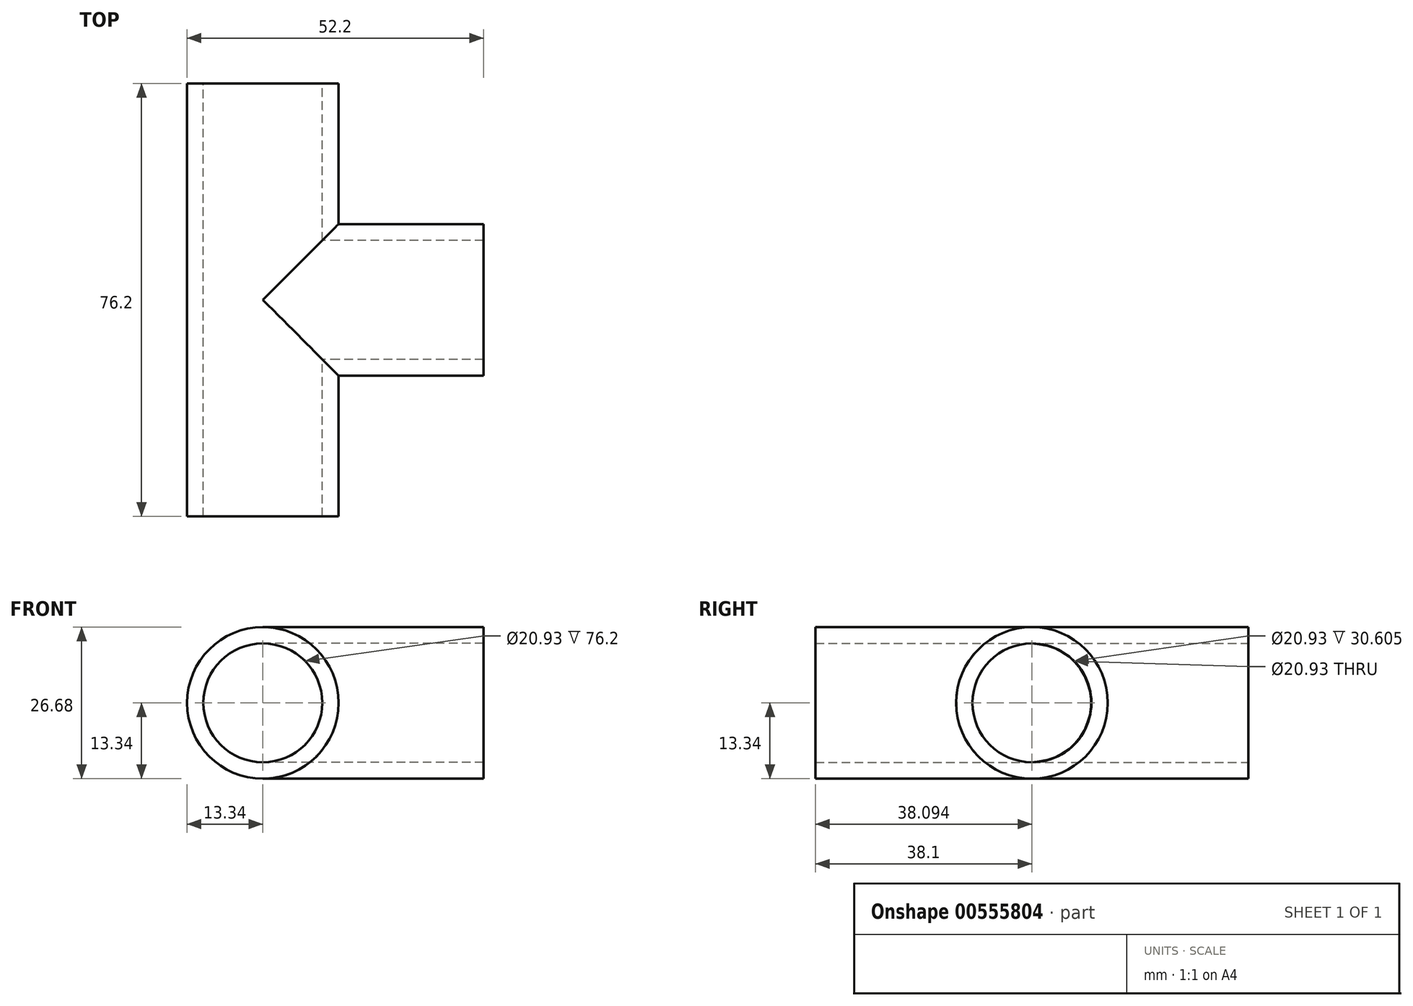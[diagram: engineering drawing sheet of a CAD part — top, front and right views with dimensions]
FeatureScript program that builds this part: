
annotation { "Feature Type Name" : "Feature", "Feature Type Description" : "" }
export const myFeature = defineFeature(function(context is Context, id is Id, definition is map)
    precondition{}
    {
        {
            var Q0;
            Q0=qCreatedBy(makeId("Front.planeOp"),FACE);
            var sketch = newSketch(context, id + "F0", { "sketchPlane" : qUnion([Q0])});
            skCircle(sketch, "E0", {"center": v(0, 0) * mm, "radius": 13.33 * mm});
            skCircle(sketch, "E1", {"center": v(0, 0) * mm, "radius": 10.46 * mm});
            skSolve(sketch);
        }
        {
            var Q0;
            Q0=qCreatedBy(makeId("Right.planeOp"),FACE);
            var sketch = newSketch(context, id + "F1", { "sketchPlane" : qUnion([Q0])});
            skLineSegment(sketch, "E2", {"start": v(0, 0) * mm, "end": v(76.2, 0) * mm});
            skSolve(sketch);
        }
        {
            var Q0;
            Q0=makeQuery(id+"F0.imprint","IMPRINT",FACE,{"disambiguationData":[TD([[makeQuery(id+"F0.imprint","IMPRINT",EDGE,{"derivedFrom":sQuery(id+"F0.wireOp",EDGE,"E0")}),1.0]])]});
            var Q1;
            Q1=sQuery(id+"F1.wireOp",EDGE,"E2");
            sweep(context, id + "F2", {"profiles" : qUnion([Q0]), "path" : qUnion([Q1])});
        }
        {
            var Q0;
            Q0=qCreatedBy(makeId("Right.planeOp"),FACE);
            var sketch = newSketch(context, id + "F3", { "sketchPlane" : qUnion([Q0])});
            skLineSegment(sketch, "E3.left", {"start": v(76.19, -14.7) * mm, "end": v(76.19, 11.97) * mm, "construction": true});
            skPoint(sketch, "E3.middle", {"position": v(0, 0) * mm});
            skLineSegment(sketch, "E4", {"start": v(0, -13.33) * mm, "end": v(0, 13.34) * mm, "construction": true});
            skPoint(sketch, "E3.right.end.orphan", {"position": v(-76.19, 14.7) * mm});
            skPoint(sketch, "E3.right.start.orphan", {"position": v(-76.19, -11.97) * mm});
            skLineSegment(sketch, "E5", {"start": v(0, -13.33) * mm, "end": v(76.19, -13.33) * mm, "construction": true});
            skLineSegment(sketch, "E6", {"start": v(0, 13.34) * mm, "end": v(76.2, 13.34) * mm, "construction": true});
            skLineSegment(sketch, "E7", {"start": v(76.2, 13.34) * mm, "end": v(76.19, -13.33) * mm, "construction": true});
            skLineSegment(sketch, "E8", {"start": v(0, 0) * mm, "end": v(76.19, 0) * mm, "construction": true});
            skCircle(sketch, "E9", {"center": v(38.1, 0) * mm, "radius": 10.46 * mm});
            skSolve(sketch);
        }
        {
            var Q0;
            Q0 = qSketchRegion(id + "F3", true);
            extrude(context, id + "F4", {"entities" : qUnion([Q0]), "operationType" : NewBodyOperationType.REMOVE, "depth" : 24.13 * mm, "offsetDistance" : 25.4 * mm});
        }
        {
            var Q0;
            Q0=qCreatedBy(makeId("Right.planeOp"),FACE);
            var sketch = newSketch(context, id + "F5", { "sketchPlane" : qUnion([Q0])});
            skLineSegment(sketch, "E10.bottom", {"start": v(76.2, -13.33) * mm, "end": v(0, -13.34) * mm, "construction": true});
            skLineSegment(sketch, "E10.top", {"start": v(76.2, 13.34) * mm, "end": v(0, 13.34) * mm, "construction": true});
            skLineSegment(sketch, "E10.left", {"start": v(76.2, -13.33) * mm, "end": v(76.2, 13.34) * mm, "construction": true});
            skPoint(sketch, "E10.middle", {"position": v(0, 0) * mm});
            skLineSegment(sketch, "E11", {"start": v(0, -13.34) * mm, "end": v(0, 13.34) * mm, "construction": true});
            skLineSegment(sketch, "E12", {"start": v(0, 13.34) * mm, "end": v(0, 0) * mm, "construction": true});
            skLineSegment(sketch, "E13", {"start": v(76.2, 0) * mm, "end": v(0, 0) * mm, "construction": true});
            skPoint(sketch, "E10.right.end.orphan", {"position": v(-76.2, 13.33) * mm});
            skPoint(sketch, "E10.right.start.orphan", {"position": v(-76.2, -13.34) * mm});
            skCircle(sketch, "E14", {"center": v(38.1, 0) * mm, "radius": 13.34 * mm});
            skCircle(sketch, "E15", {"center": v(38.1, 0) * mm, "radius": 10.46 * mm});
            skSolve(sketch);
        }
        {
            var Q0;
            Q0 = qSketchRegion(id + "F5", true);
            extrude(context, id + "F6", {"entities" : qUnion([Q0]), "operationType" : NewBodyOperationType.ADD, "depth" : 38.86 * mm, "offsetDistance" : 25.4 * mm});
        }
        {
            var Q0;
            Q0=qCreatedBy(makeId("Front.planeOp"),FACE);
            var sketch = newSketch(context, id + "F7", { "sketchPlane" : qUnion([Q0])});
            skCircle(sketch, "E16", {"center": v(0, 0) * mm, "radius": 10.46 * mm});
            skSolve(sketch);
        }
        {
            var Q0;
            Q0 = qSketchRegion(id + "F7", true);
            extrude(context, id + "F8", {"entities" : qUnion([Q0]), "operationType" : NewBodyOperationType.REMOVE, "oppositeDirection" : true, "depth" : 91.7 * mm, "offsetDistance" : 25.4 * mm});
        }
    });
